# Revit family: R 8 (a)
name_source: partatom
category: Equipement spécialisé
revit_build: Autodesk Revit LT 2015 (Build: 20140606_1530(x64)
units: mm (PartAtom-declared; Revit-internal decimal feet)

## types (5) — shared parameters
Apparent Power = 0 VA
Depth = 580 mm
Description = CUTTERS DE TABLE
Electrique connexion = 110 mm
Fabricant = ROBOT COUPE
Height = 585 mm
Phase = 3
UP Delpth = 705 mm
UP Height = 835 mm
URL = www.robot-coupe.com
Width = 395 mm
water = Connector
zero-valued in all types: Cold water supply, Cold water supply height, Used water, Waste water height

## per-type parameters (varying)
| type | Amps | Cycle | HP | Modèle | Speeds (Rpm) | Volts | Watts | Weight |
| R 8   230/50/3 | 4.8 & 8.5 A | 50 Hz |  | R 8 | 1500 & 3000 | 230 V | 2200 W | 44.9 kg |
| R 8   400/50/3 | 5.5 & 10 A | 50 Hz |  | R 8 | 1500 & 3000 | 400 V | 2200 W | 44.9 kg |
| R 8   220/60/3 | 5.5 & 10 A | 60 Hz |  | R 8 | 1500 & 3000 | 220 V | 2200 W | 44.9 kg |
| R 8   380/60/3 | 6 & 11 A | 60 Hz |  | R 8 | 1500 & 3000 | 380 V | 2200 W | 44.9 kg |
| R 8 USA    208-240/60/3 |  | 60 Hz | 3 | R 8 USA | 1800 & 3600 | 208 V | 0 W | 100 lbs |

## geometry (parser evidence)
native form markers: Blend x104, Sweep x5
no freeform markers — native parametric forms only
